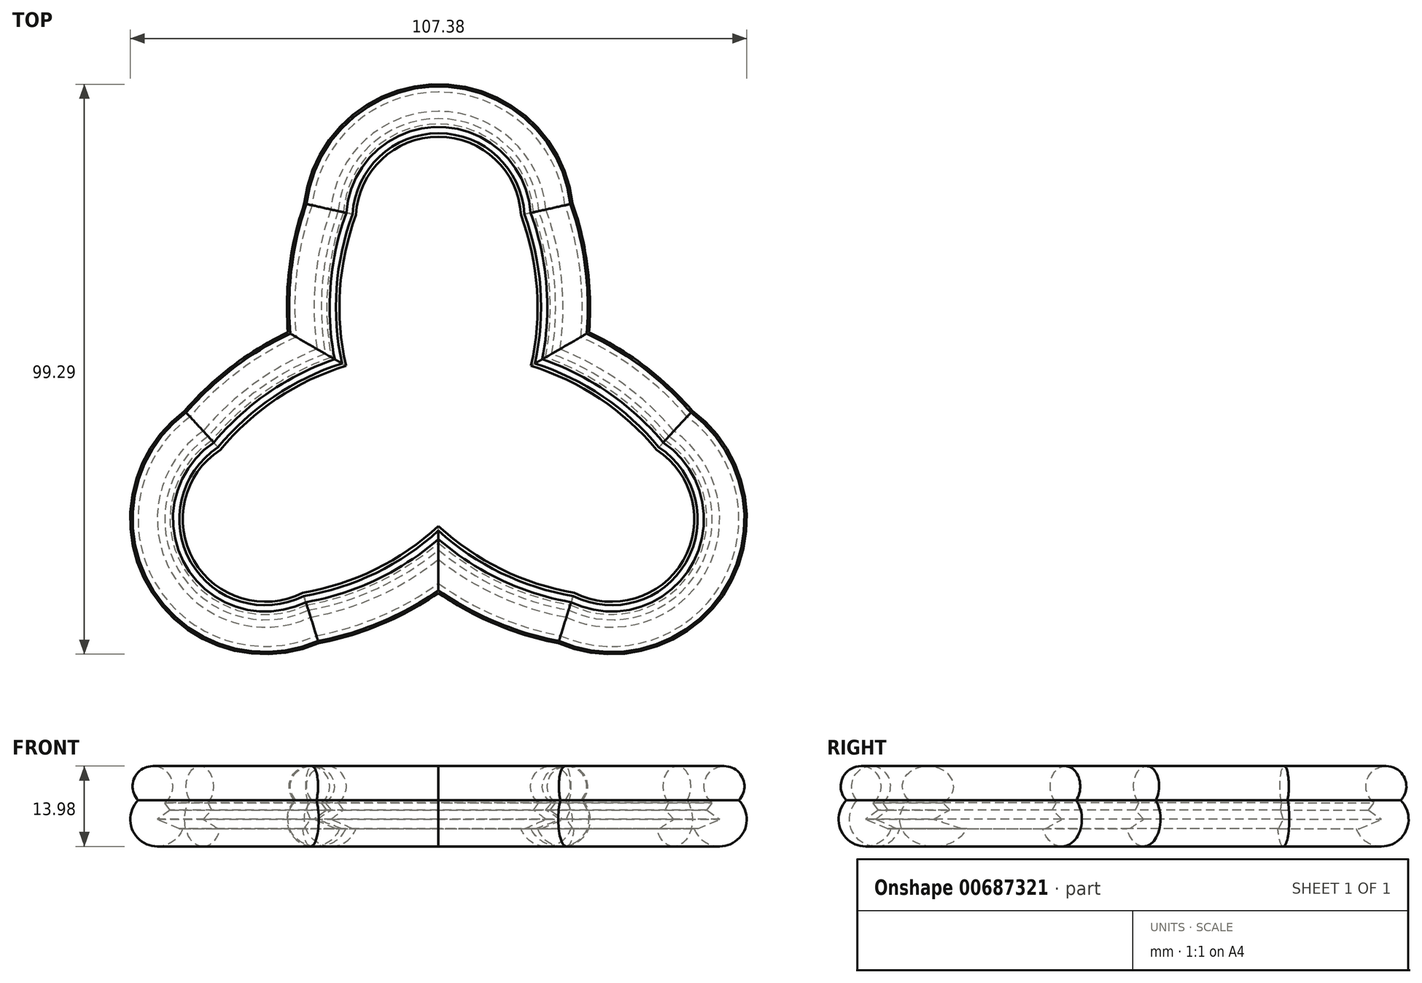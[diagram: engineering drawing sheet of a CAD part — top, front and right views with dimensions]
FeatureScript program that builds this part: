
annotation { "Feature Type Name" : "Feature", "Feature Type Description" : "" }
export const myFeature = defineFeature(function(context is Context, id is Id, definition is map)
    precondition{}
    {
        {
            var Q0;
            Q0=qCreatedBy(makeId("Top.planeOp"),FACE);
            var sketch = newSketch(context, id + "F0", { "sketchPlane" : qUnion([Q0])});
            skArc(sketch, "E0", {"start": v(10.49, 34.83) * mm, "mid": v(0, 45.31) * mm, "end": v(-10.49, 34.83) * mm});
            skCircle(sketch, "E1", {"center": v(0, 0) * mm, "radius": 8.57 * mm});
            skArc(sketch, "E2", {"start": v(-10.49, 34.83) * mm, "mid": v(-13.34, 20.75) * mm, "end": v(-11.3, 6.53) * mm});
            skLineSegment(sketch, "E3", {"start": v(0, 0) * mm, "end": v(0, 34.83) * mm, "construction": true});
            skArc(sketch, "E4.MirrorCS", {"start": v(10.49, 34.83) * mm, "mid": v(13.34, 20.75) * mm, "end": v(11.3, 6.53) * mm});
            skArc(sketch, "E5.1.0", {"start": v(-35.4, -8.33) * mm, "mid": v(-39.24, -22.66) * mm, "end": v(-24.92, -26.5) * mm});
            skArc(sketch, "E5.1.1", {"start": v(-24.92, -26.5) * mm, "mid": v(-11.3, -21.93) * mm, "end": v(0, -13.05) * mm});
            skArc(sketch, "E5.1.2", {"start": v(-35.4, -8.33) * mm, "mid": v(-24.64, 1.18) * mm, "end": v(-11.3, 6.53) * mm});
            skArc(sketch, "E5.2.0", {"start": v(24.92, -26.5) * mm, "mid": v(39.24, -22.66) * mm, "end": v(35.4, -8.33) * mm});
            skArc(sketch, "E5.2.1", {"start": v(35.4, -8.33) * mm, "mid": v(24.64, 1.18) * mm, "end": v(11.3, 6.53) * mm});
            skArc(sketch, "E5.2.2", {"start": v(24.92, -26.5) * mm, "mid": v(11.3, -21.93) * mm, "end": v(0, -13.05) * mm});
            skLineSegment(sketch, "E6", {"start": v(0, 34.83) * mm, "end": v(0, 45.31) * mm, "construction": true});
            skPoint(sketch, "E7", {"position": v(0, 45.31) * mm});
            skPoint(sketch, "E8.orphan", {"position": v(4.28, -7.42) * mm});
            skPoint(sketch, "E9.orphan", {"position": v(-4.28, -7.42) * mm});
            skPoint(sketch, "E10.orphan", {"position": v(-8.57, 0) * mm});
            skPoint(sketch, "E11.orphan", {"position": v(-4.28, 7.42) * mm});
            skPoint(sketch, "E12.orphan", {"position": v(4.28, 7.42) * mm});
            skPoint(sketch, "E13.orphan", {"position": v(8.57, 0) * mm});
            skSolve(sketch);
        }
        {
            var Q0;
            Q0=qCreatedBy(makeId("Right.planeOp"),FACE);
            var sketch = newSketch(context, id + "F1", { "sketchPlane" : qUnion([Q0])});
            skLineSegment(sketch, "E14.bottom", {"start": v(45.88, 9.15) * mm, "end": v(49.82, 9.15) * mm});
            skLineSegment(sketch, "E14.top", {"start": v(45.88, -1.63) * mm, "end": v(49.82, -1.63) * mm});
            skLineSegment(sketch, "E14.left", {"start": v(45.88, 9.15) * mm, "end": v(45.88, -1.63) * mm});
            skLineSegment(sketch, "E14.right", {"start": v(49.82, 9.15) * mm, "end": v(49.82, -1.63) * mm});
            skLineSegment(sketch, "E15", {"start": v(49.82, 9.15) * mm, "end": v(54.44, 5.75) * mm});
            skLineSegment(sketch, "E16", {"start": v(54.44, 5.75) * mm, "end": v(51.42, 1.63) * mm});
            skLineSegment(sketch, "E17", {"start": v(51.42, 1.63) * mm, "end": v(53.64, 0) * mm});
            skLineSegment(sketch, "E18", {"start": v(53.64, 0) * mm, "end": v(49.82, -1.63) * mm});
            skCircle(sketch, "E19", {"center": v(54.44, 5.75) * mm, "radius": 3.53 * mm});
            skCircle(sketch, "E20", {"center": v(53.64, 0) * mm, "radius": 4.71 * mm});
            skSolve(sketch);
        }
        {
            var Q0;
            {var subQ0=sQuery(id+"F1.wireOp",EDGE,"E20");var subQ1=sQuery(id+"F1.wireOp",EDGE,"E16");var subQ2=makeQuery(id+"F1.imprint","INTERSECT",VERTEX,{"derivedFrom":[subQ1,subQ0]});Q0=makeQuery(id+"F1.imprint","IMPRINT",FACE,{"disambiguationData":[TD([[makeQuery(id+"F1.imprint","IMPRINT",EDGE,{"disambiguationData":[TD([[subQ2,-1.0]])],"derivedFrom":subQ1}),-1.0]])]});}
            var Q1;
            {var subQ0=sQuery(id+"F1.wireOp",EDGE,"E17");Q1=makeQuery(id+"F1.imprint","IMPRINT",FACE,{"disambiguationData":[TD([[makeQuery(id+"F1.imprint","IMPRINT",EDGE,{"derivedFrom":subQ0}),1.0]])]});}
            var Q2;
            {var subQ0=sQuery(id+"F1.wireOp",EDGE,"E20");var subQ1=sQuery(id+"F1.wireOp",EDGE,"E16");var subQ2=makeQuery(id+"F1.imprint","INTERSECT",VERTEX,{"derivedFrom":[subQ1,subQ0]});Q2=makeQuery(id+"F1.imprint","IMPRINT",FACE,{"disambiguationData":[TD([[makeQuery(id+"F1.imprint","IMPRINT",EDGE,{"disambiguationData":[TD([[subQ2,-1.0]])],"derivedFrom":subQ1}),1.0]])]});}
            var Q3;
            {var subQ0=sQuery(id+"F1.wireOp",EDGE,"E16");var subQ1=sQuery(id+"F1.wireOp",EDGE,"E15");var subQ2=makeQuery(id+"F1.imprint","INTERSECT",VERTEX,{"derivedFrom":[subQ1,subQ0]});Q3=makeQuery(id+"F1.imprint","IMPRINT",FACE,{"disambiguationData":[TD([[makeQuery(id+"F1.imprint","IMPRINT",EDGE,{"disambiguationData":[TD([[subQ2,1.0]])],"derivedFrom":subQ1}),1.0]])]});}
            var Q4;
            {var subQ0=sQuery(id+"F1.wireOp",EDGE,"E16");var subQ1=sQuery(id+"F1.wireOp",EDGE,"E15");var subQ2=makeQuery(id+"F1.imprint","INTERSECT",VERTEX,{"derivedFrom":[subQ1,subQ0]});Q4=makeQuery(id+"F1.imprint","IMPRINT",FACE,{"disambiguationData":[TD([[makeQuery(id+"F1.imprint","IMPRINT",EDGE,{"disambiguationData":[TD([[subQ2,1.0]])],"derivedFrom":subQ1}),-1.0]])]});}
            var Q5;
            Q5=sQuery(id+"F0.wireOp",EDGE,"E0");
            var Q6;
            Q6=sQuery(id+"F0.wireOp",EDGE,"E4.MirrorCS");
            var Q7;
            Q7=sQuery(id+"F0.wireOp",EDGE,"E5.2.1");
            var Q8;
            Q8=sQuery(id+"F0.wireOp",EDGE,"E5.2.0");
            var Q9;
            Q9=sQuery(id+"F0.wireOp",EDGE,"E5.2.2");
            var Q10;
            Q10=sQuery(id+"F0.wireOp",EDGE,"E5.1.1");
            var Q11;
            Q11=sQuery(id+"F0.wireOp",EDGE,"E5.1.0");
            var Q12;
            Q12=sQuery(id+"F0.wireOp",EDGE,"E5.1.2");
            var Q13;
            Q13=sQuery(id+"F0.wireOp",EDGE,"E2");
            sweep(context, id + "F2", {"profiles" : qUnion([Q0, Q1, Q2, Q3, Q4]), "path" : qUnion([Q5, Q6, Q7, Q8, Q9, Q10, Q11, Q12, Q13])});
        }
    });
